annotation { "Feature Type Name" : "Feature", "Feature Type Description" : "" }
export const myFeature = defineFeature(function(context is Context, id is Id, definition is map)
    precondition{}
    {
        {
            var Q0;
            Q0=qCreatedBy(makeId("Top.planeOp"),FACE);
            var sketch = newSketch(context, id + "F0", { "sketchPlane" : qUnion([Q0])});
            skLineSegment(sketch, "E0.bottom", {"start": v(0, 0) * mm, "end": v(66.68, 0) * mm});
            skLineSegment(sketch, "E0.top", {"start": v(0, -53.98) * mm, "end": v(66.68, -53.98) * mm});
            skLineSegment(sketch, "E0.left", {"start": v(0, 0) * mm, "end": v(0, -53.98) * mm});
            skLineSegment(sketch, "E0.right", {"start": v(66.68, 0) * mm, "end": v(66.68, -53.97) * mm});
            skLineSegment(sketch, "E1.bottom", {"start": v(-2.38, -7.94) * mm, "end": v(5.56, -7.94) * mm});
            skLineSegment(sketch, "E1.top", {"start": v(-2.38, -15.08) * mm, "end": v(5.56, -15.08) * mm});
            skLineSegment(sketch, "E1.left", {"start": v(-2.38, -7.94) * mm, "end": v(-2.38, -15.08) * mm});
            skLineSegment(sketch, "E1.right", {"start": v(5.56, -7.94) * mm, "end": v(5.56, -15.08) * mm});
            skLineSegment(sketch, "E2", {"start": v(66.68, -12.7) * mm, "end": v(70.64, -16.67) * mm});
            skLineSegment(sketch, "E3", {"start": v(70.64, -16.67) * mm, "end": v(70.64, -48.42) * mm});
            skLineSegment(sketch, "E4", {"start": v(70.64, -48.42) * mm, "end": v(66.68, -52.39) * mm});
            skCircle(sketch, "E5", {"center": v(68.26, -19.05) * mm, "radius": 1.98 * mm});
            skLineSegment(sketch, "E6", {"start": v(66.68, -12.7) * mm, "end": v(68.26, -12.7) * mm, "construction": true});
            skLineSegment(sketch, "E7", {"start": v(68.26, -12.7) * mm, "end": v(68.26, -19.05) * mm, "construction": true});
            skLineSegment(sketch, "E8", {"start": v(70.64, -32.54) * mm, "end": v(66.68, -32.54) * mm});
            skCircle(sketch, "E9.MirrorC", {"center": v(68.26, -46.04) * mm, "radius": 1.98 * mm});
            skCircle(sketch, "E10", {"center": v(15.88, -2.38) * mm, "radius": 1.98 * mm});
            skLineSegment(sketch, "E11", {"start": v(0, -26.99) * mm, "end": v(15.88, -26.99) * mm, "construction": true});
            skCircle(sketch, "E12.MirrorC", {"center": v(15.88, -51.6) * mm, "radius": 1.98 * mm});
            skSolve(sketch);
        }
        {
            var Q0;
            {var subQ9=sQuery(id+"F0.wireOp",EDGE,"E0.bottom");Q0=makeQuery(id+"F0.imprint","IMPRINT",FACE,{"disambiguationData":[TD([[makeQuery(id+"F0.imprint","IMPRINT",EDGE,{"derivedFrom":subQ9}),-1.0]])]});}
            var Q1;
            {var subQ5=sQuery(id+"F0.wireOp",EDGE,"E2");Q1=makeQuery(id+"F0.imprint","IMPRINT",FACE,{"disambiguationData":[TD([[makeQuery(id+"F0.imprint","IMPRINT",EDGE,{"derivedFrom":subQ5}),-1.0]])]});}
            var Q2;
            {var subQ0=sQuery(id+"F0.wireOp",EDGE,"E4");Q2=makeQuery(id+"F0.imprint","IMPRINT",FACE,{"disambiguationData":[TD([[makeQuery(id+"F0.imprint","IMPRINT",EDGE,{"derivedFrom":subQ0}),-1.0]])]});}
            extrude(context, id + "F1", {"entities" : qUnion([Q0, Q1, Q2]), "depth" : 1.59 * mm});
        }
        {
            var Q0;
            {var subQ5=sQuery(id+"F0.wireOp",EDGE,"E1.right");Q0=makeQuery(id+"F0.imprint","IMPRINT",FACE,{"disambiguationData":[TD([[makeQuery(id+"F0.imprint","IMPRINT",EDGE,{"derivedFrom":subQ5}),-1.0]])]});}
            var Q1;
            {var subQ5=sQuery(id+"F0.wireOp",EDGE,"E1.left");Q1=makeQuery(id+"F0.imprint","IMPRINT",FACE,{"disambiguationData":[TD([[makeQuery(id+"F0.imprint","IMPRINT",EDGE,{"derivedFrom":subQ5}),1.0]])]});}
            extrude(context, id + "F2", {"entities" : qUnion([Q0, Q1]), "operationType" : NewBodyOperationType.ADD, "depth" : 5.16 * mm});
        }
        {
            var Q0;
            Q0=makeQuery(id+"F1.opExtrude","CAP_FACE",FACE,{"disambiguationData":[OSD([sQuery(id+"F0.wireOp",EDGE,"E0.bottom"),sQuery(id+"F0.wireOp",EDGE,"E0.top"),sQuery(id+"F0.wireOp",EDGE,"E0.left"),sQuery(id+"F0.wireOp",EDGE,"E0.right"),sQuery(id+"F0.wireOp",EDGE,"E1.bottom"),sQuery(id+"F0.wireOp",EDGE,"E1.top"),sQuery(id+"F0.wireOp",EDGE,"E1.right"),sQuery(id+"F0.wireOp",EDGE,"E2"),sQuery(id+"F0.wireOp",EDGE,"E3"),sQuery(id+"F0.wireOp",EDGE,"E4"),sQuery(id+"F0.wireOp",EDGE,"E5"),sQuery(id+"F0.wireOp",EDGE,"E9.MirrorC"),sQuery(id+"F0.wireOp",EDGE,"E10"),sQuery(id+"F0.wireOp",EDGE,"E12.MirrorC")])],"isStart":false});
            var sketch = newSketch(context, id + "F3", { "sketchPlane" : qUnion([Q0])});
            skLineSegment(sketch, "E13.bottom", {"start": v(31.75, -50) * mm, "end": v(46.83, -50) * mm});
            skLineSegment(sketch, "E13.top", {"start": v(31.75, -52.39) * mm, "end": v(46.83, -52.39) * mm});
            skLineSegment(sketch, "E13.left", {"start": v(31.75, -50) * mm, "end": v(31.75, -52.39) * mm});
            skLineSegment(sketch, "E13.right", {"start": v(46.83, -50) * mm, "end": v(46.83, -52.39) * mm});
            skLineSegment(sketch, "E14", {"start": v(48.02, -48.64) * mm, "end": v(48.02, -53.98) * mm, "construction": true});
            skLineSegment(sketch, "E15.MirrorCS", {"start": v(64.3, -50) * mm, "end": v(49.21, -50) * mm});
            skLineSegment(sketch, "E16.MirrorCS", {"start": v(49.21, -50) * mm, "end": v(49.21, -52.39) * mm});
            skLineSegment(sketch, "E17.MirrorCS", {"start": v(64.3, -52.39) * mm, "end": v(49.21, -52.39) * mm});
            skLineSegment(sketch, "E18.MirrorCS", {"start": v(64.3, -50) * mm, "end": v(64.3, -52.39) * mm});
            skLineSegment(sketch, "E19.bottom", {"start": v(32.35, -50.4) * mm, "end": v(33.93, -50.4) * mm});
            skLineSegment(sketch, "E19.top", {"start": v(32.35, -52) * mm, "end": v(33.93, -52) * mm});
            skLineSegment(sketch, "E19.left", {"start": v(32.35, -50.4) * mm, "end": v(32.35, -52) * mm});
            skLineSegment(sketch, "E19.right", {"start": v(33.93, -50.4) * mm, "end": v(33.93, -52) * mm});
            skLineSegment(sketch, "E20.bottom", {"start": v(34.77, -50.4) * mm, "end": v(36.36, -50.4) * mm});
            skLineSegment(sketch, "E20.top", {"start": v(34.77, -52) * mm, "end": v(36.36, -52) * mm});
            skLineSegment(sketch, "E20.left", {"start": v(34.77, -50.4) * mm, "end": v(34.77, -52) * mm});
            skLineSegment(sketch, "E20.right", {"start": v(36.36, -50.4) * mm, "end": v(36.36, -52) * mm});
            skLineSegment(sketch, "E21", {"start": v(36.8, -50) * mm, "end": v(36.8, -52.39) * mm, "construction": true});
            skLineSegment(sketch, "E22.MirrorCS", {"start": v(38.8, -50.4) * mm, "end": v(37.22, -50.4) * mm});
            skLineSegment(sketch, "E23.MirrorCS", {"start": v(37.22, -50.4) * mm, "end": v(37.22, -52) * mm});
            skLineSegment(sketch, "E24.MirrorCS", {"start": v(38.8, -52) * mm, "end": v(37.22, -52) * mm});
            skLineSegment(sketch, "E25.MirrorCS", {"start": v(38.8, -50.4) * mm, "end": v(38.8, -52) * mm});
            skLineSegment(sketch, "E26.MirrorCS", {"start": v(39.65, -50.4) * mm, "end": v(39.65, -52) * mm});
            skLineSegment(sketch, "E27.MirrorCS", {"start": v(41.24, -50.4) * mm, "end": v(39.65, -50.4) * mm});
            skLineSegment(sketch, "E28.MirrorCS", {"start": v(41.24, -50.4) * mm, "end": v(41.24, -52) * mm});
            skLineSegment(sketch, "E29.MirrorCS", {"start": v(41.24, -52) * mm, "end": v(39.65, -52) * mm});
            skLineSegment(sketch, "E30", {"start": v(41.67, -50) * mm, "end": v(41.67, -52.39) * mm, "construction": true});
            skLineSegment(sketch, "E31.MirrorCS", {"start": v(42.1, -50.4) * mm, "end": v(43.69, -50.4) * mm});
            skLineSegment(sketch, "E32.MirrorCS", {"start": v(42.1, -50.4) * mm, "end": v(42.1, -52) * mm});
            skLineSegment(sketch, "E33.MirrorCS", {"start": v(42.1, -52) * mm, "end": v(43.69, -52) * mm});
            skLineSegment(sketch, "E34.MirrorCS", {"start": v(43.69, -50.4) * mm, "end": v(43.69, -52) * mm});
            skLineSegment(sketch, "E35.MirrorCS", {"start": v(44.52, -50.4) * mm, "end": v(44.52, -52) * mm});
            skLineSegment(sketch, "E36.MirrorCS", {"start": v(44.52, -50.4) * mm, "end": v(46.11, -50.4) * mm});
            skLineSegment(sketch, "E37.MirrorCS", {"start": v(46.11, -50.4) * mm, "end": v(46.11, -52) * mm});
            skLineSegment(sketch, "E38.MirrorCS", {"start": v(44.52, -52) * mm, "end": v(46.11, -52) * mm});
            skLineSegment(sketch, "E39.MirrorCS", {"start": v(49.93, -50.4) * mm, "end": v(49.93, -52) * mm});
            skLineSegment(sketch, "E40.MirrorCS", {"start": v(51.52, -50.4) * mm, "end": v(49.93, -50.4) * mm});
            skLineSegment(sketch, "E41.MirrorCS", {"start": v(51.52, -50.4) * mm, "end": v(51.52, -52) * mm});
            skLineSegment(sketch, "E42.MirrorCS", {"start": v(51.52, -52) * mm, "end": v(49.93, -52) * mm});
            skLineSegment(sketch, "E43.MirrorCS", {"start": v(52.36, -50.4) * mm, "end": v(52.36, -52) * mm});
            skLineSegment(sketch, "E44.MirrorCS", {"start": v(53.94, -50.4) * mm, "end": v(52.36, -50.4) * mm});
            skLineSegment(sketch, "E45.MirrorCS", {"start": v(53.94, -50.4) * mm, "end": v(53.94, -52) * mm});
            skLineSegment(sketch, "E46.MirrorCS", {"start": v(53.94, -52) * mm, "end": v(52.36, -52) * mm});
            skLineSegment(sketch, "E47.MirrorCS", {"start": v(54.8, -50.4) * mm, "end": v(56.4, -50.4) * mm});
            skLineSegment(sketch, "E48.MirrorCS", {"start": v(54.8, -50.4) * mm, "end": v(54.8, -52) * mm});
            skLineSegment(sketch, "E49.MirrorCS", {"start": v(54.8, -52) * mm, "end": v(56.4, -52) * mm});
            skLineSegment(sketch, "E50.MirrorCS", {"start": v(56.4, -50.4) * mm, "end": v(56.4, -52) * mm});
            skLineSegment(sketch, "E51.MirrorCS", {"start": v(57.23, -50.4) * mm, "end": v(57.23, -52) * mm});
            skLineSegment(sketch, "E52.MirrorCS", {"start": v(57.23, -50.4) * mm, "end": v(58.82, -50.4) * mm});
            skLineSegment(sketch, "E53.MirrorCS", {"start": v(58.82, -50.4) * mm, "end": v(58.82, -52) * mm});
            skLineSegment(sketch, "E54.MirrorCS", {"start": v(57.23, -52) * mm, "end": v(58.82, -52) * mm});
            skLineSegment(sketch, "E55.MirrorCS", {"start": v(59.69, -50.4) * mm, "end": v(59.69, -52) * mm});
            skLineSegment(sketch, "E56.MirrorCS", {"start": v(61.27, -50.4) * mm, "end": v(59.69, -50.4) * mm});
            skLineSegment(sketch, "E57.MirrorCS", {"start": v(61.27, -50.4) * mm, "end": v(61.27, -52) * mm});
            skLineSegment(sketch, "E58.MirrorCS", {"start": v(61.27, -52) * mm, "end": v(59.69, -52) * mm});
            skLineSegment(sketch, "E59.MirrorCS", {"start": v(62.11, -50.4) * mm, "end": v(62.11, -52) * mm});
            skLineSegment(sketch, "E60.MirrorCS", {"start": v(63.7, -50.4) * mm, "end": v(62.11, -50.4) * mm});
            skLineSegment(sketch, "E61.MirrorCS", {"start": v(63.7, -50.4) * mm, "end": v(63.7, -52) * mm});
            skLineSegment(sketch, "E62.MirrorCS", {"start": v(63.7, -52) * mm, "end": v(62.11, -52) * mm});
            skSolve(sketch);
        }
        {
            var Q0;
            Q0=makeQuery(id+"F3.imprint","IMPRINT",FACE,{"disambiguationData":[TD([[makeQuery(id+"F3.imprint","IMPRINT",EDGE,{"derivedFrom":sQuery(id+"F3.wireOp",EDGE,"E13.bottom")}),-1.0]])]});
            var Q1;
            Q1=makeQuery(id+"F3.imprint","IMPRINT",FACE,{"disambiguationData":[TD([[makeQuery(id+"F3.imprint","IMPRINT",EDGE,{"derivedFrom":sQuery(id+"F3.wireOp",EDGE,"E15.MirrorCS")}),1.0]])]});
            extrude(context, id + "F4", {"entities" : qUnion([Q0, Q1]), "operationType" : NewBodyOperationType.ADD, "depth" : 7.94 * mm});
        }
        {
            var Q0;
            {var subQ0=sQuery(id+"F0.wireOp",EDGE,"E1.right");var subQ1=sQuery(id+"F0.wireOp",EDGE,"E0.left");var subQ2=sQuery(id+"F0.wireOp",EDGE,"E0.bottom");var subQ3=sQuery(id+"F0.wireOp",EDGE,"E1.bottom");var subQ4=sQuery(id+"F0.wireOp",EDGE,"E1.top");var subQ5=sQuery(id+"F0.wireOp",EDGE,"E12.MirrorC");var subQ6=sQuery(id+"F0.wireOp",EDGE,"E10");var subQ7=sQuery(id+"F0.wireOp",EDGE,"E9.MirrorC");var subQ8=sQuery(id+"F0.wireOp",EDGE,"E0.top");var subQ9=sQuery(id+"F0.wireOp",EDGE,"E3");var subQ10=sQuery(id+"F0.wireOp",EDGE,"E0.right");var subQ11=sQuery(id+"F0.wireOp",EDGE,"E2");var subQ12=sQuery(id+"F0.wireOp",EDGE,"E4");var subQ13=sQuery(id+"F0.wireOp",EDGE,"E5");Q0=makeQuery(id+"F4.boolean.opBoolean","SPLIT",FACE,{"disambiguationData":[TD([makeQuery(id+"F1.opExtrude","SWEPT_FACE",FACE,{"disambiguationData":[OSD([subQ2])]})])],"derivedFrom":makeQuery(id+"F1.opExtrude","CAP_FACE",FACE,{"disambiguationData":[OSD([subQ2,subQ8,subQ1,subQ10,subQ3,subQ4,subQ0,subQ11,subQ9,subQ12,subQ13,subQ7,subQ6,subQ5])],"isStart":false})});}
            var sketch = newSketch(context, id + "F5", { "sketchPlane" : qUnion([Q0])});
            skLineSegment(sketch, "E63.bottom", {"start": v(30.96, -34.13) * mm, "end": v(65.88, -34.13) * mm});
            skLineSegment(sketch, "E63.top", {"start": v(30.96, -42.86) * mm, "end": v(65.88, -42.86) * mm});
            skLineSegment(sketch, "E63.left", {"start": v(30.96, -34.13) * mm, "end": v(30.96, -42.86) * mm});
            skLineSegment(sketch, "E63.right", {"start": v(65.88, -34.13) * mm, "end": v(65.88, -42.86) * mm});
            skSolve(sketch);
        }
        {
            var Q0;
            Q0=makeQuery(id+"F5.imprint","IMPRINT",FACE,{"disambiguationData":[TD([[makeQuery(id+"F5.imprint","IMPRINT",EDGE,{"derivedFrom":sQuery(id+"F5.wireOp",EDGE,"E63.bottom")}),-1.0]])]});
            extrude(context, id + "F6", {"entities" : qUnion([Q0]), "operationType" : NewBodyOperationType.ADD, "depth" : 7.14 * mm});
        }
        {
            var Q0;
            {var subQ0=sQuery(id+"F0.wireOp",EDGE,"E1.right");var subQ1=sQuery(id+"F0.wireOp",EDGE,"E0.left");var subQ2=sQuery(id+"F0.wireOp",EDGE,"E0.bottom");var subQ3=sQuery(id+"F0.wireOp",EDGE,"E1.bottom");var subQ4=sQuery(id+"F0.wireOp",EDGE,"E1.top");var subQ5=sQuery(id+"F0.wireOp",EDGE,"E12.MirrorC");var subQ6=sQuery(id+"F0.wireOp",EDGE,"E10");var subQ7=sQuery(id+"F0.wireOp",EDGE,"E9.MirrorC");var subQ8=sQuery(id+"F0.wireOp",EDGE,"E0.top");var subQ9=sQuery(id+"F0.wireOp",EDGE,"E3");var subQ10=sQuery(id+"F0.wireOp",EDGE,"E0.right");var subQ11=sQuery(id+"F0.wireOp",EDGE,"E2");var subQ12=sQuery(id+"F0.wireOp",EDGE,"E4");var subQ13=sQuery(id+"F0.wireOp",EDGE,"E5");Q0=makeQuery(id+"F4.boolean.opBoolean","SPLIT",FACE,{"disambiguationData":[TD([makeQuery(id+"F1.opExtrude","SWEPT_FACE",FACE,{"disambiguationData":[OSD([subQ2])]})])],"derivedFrom":makeQuery(id+"F1.opExtrude","CAP_FACE",FACE,{"disambiguationData":[OSD([subQ2,subQ8,subQ1,subQ10,subQ3,subQ4,subQ0,subQ11,subQ9,subQ12,subQ13,subQ7,subQ6,subQ5])],"isStart":false})});}
            var sketch = newSketch(context, id + "F7", { "sketchPlane" : qUnion([Q0])});
            skLineSegment(sketch, "E64.bottom", {"start": v(53.98, -25.4) * mm, "end": v(59.53, -25.4) * mm});
            skLineSegment(sketch, "E64.top", {"start": v(53.98, -30.96) * mm, "end": v(59.53, -30.96) * mm});
            skLineSegment(sketch, "E64.left", {"start": v(53.98, -25.4) * mm, "end": v(53.98, -30.96) * mm});
            skLineSegment(sketch, "E64.right", {"start": v(59.53, -25.4) * mm, "end": v(59.53, -30.96) * mm});
            skSolve(sketch);
        }
        {
            var Q0;
            Q0=makeQuery(id+"F7.imprint","IMPRINT",FACE,{"disambiguationData":[TD([[makeQuery(id+"F7.imprint","IMPRINT",EDGE,{"derivedFrom":sQuery(id+"F7.wireOp",EDGE,"E64.bottom")}),-1.0]])]});
            extrude(context, id + "F8", {"entities" : qUnion([Q0]), "operationType" : NewBodyOperationType.ADD, "depth" : 2 / 406.4 * mm});
        }
        {
            var Q0;
            Q0=makeQuery(id+"F8.opExtrude","CAP_FACE",FACE,{"disambiguationData":[OSD([sQuery(id+"F7.wireOp",EDGE,"E64.bottom"),sQuery(id+"F7.wireOp",EDGE,"E64.top"),sQuery(id+"F7.wireOp",EDGE,"E64.left"),sQuery(id+"F7.wireOp",EDGE,"E64.right")])],"isStart":false});
            var sketch = newSketch(context, id + "F9", { "sketchPlane" : qUnion([Q0])});
            skCircle(sketch, "E65", {"center": v(56.75, -28.18) * mm, "radius": 1.98 * mm});
            skPoint(sketch, "E65.centerSnap0", {"position": v(59.53, -28.18) * mm});
            skPoint(sketch, "E65.centerSnap1", {"position": v(56.75, -25.4) * mm});
            skCircle(sketch, "E66", {"center": v(54.68, -26.1) * mm, "radius": 0.38 * mm});
            skCircle(sketch, "E67.1.0.0", {"center": v(58.8, -26.1) * mm, "radius": 0.38 * mm});
            skLineSegment(sketch, "E67.direction1", {"start": v(54.68, -26.1) * mm, "end": v(58.8, -26.1) * mm, "construction": true});
            skCircle(sketch, "E68.1.0.0", {"center": v(58.77, -30.28) * mm, "radius": 0.38 * mm});
            skLineSegment(sketch, "E68.direction1", {"start": v(58.8, -26.1) * mm, "end": v(58.77, -30.28) * mm, "construction": true});
            skCircle(sketch, "E69.1.0.0", {"center": v(54.73, -30.25) * mm, "radius": 0.38 * mm});
            skLineSegment(sketch, "E69.direction1", {"start": v(54.68, -26.1) * mm, "end": v(54.73, -30.25) * mm, "construction": true});
            skSolve(sketch);
        }
        {
            var Q0;
            Q0=makeQuery(id+"F9.imprint","IMPRINT",FACE,{"disambiguationData":[TD([[makeQuery(id+"F9.imprint","IMPRINT",EDGE,{"derivedFrom":sQuery(id+"F9.wireOp",EDGE,"E65")}),1.0]])]});
            extrude(context, id + "F10", {"entities" : qUnion([Q0]), "operationType" : NewBodyOperationType.ADD, "depth" : 0.8 * mm});
        }
        {
            var Q0;
            Q0=makeQuery(id+"F9.imprint","IMPRINT",FACE,{"disambiguationData":[TD([[makeQuery(id+"F9.imprint","IMPRINT",EDGE,{"derivedFrom":sQuery(id+"F9.wireOp",EDGE,"E66")}),1.0]])]});
            var Q1;
            Q1=makeQuery(id+"F9.imprint","IMPRINT",FACE,{"disambiguationData":[TD([[makeQuery(id+"F9.imprint","IMPRINT",EDGE,{"derivedFrom":sQuery(id+"F9.wireOp",EDGE,"E67.1.0.0")}),1.0]])]});
            var Q2;
            Q2=makeQuery(id+"F9.imprint","IMPRINT",FACE,{"disambiguationData":[TD([[makeQuery(id+"F9.imprint","IMPRINT",EDGE,{"derivedFrom":sQuery(id+"F9.wireOp",EDGE,"E68.1.0.0")}),1.0]])]});
            var Q3;
            Q3=makeQuery(id+"F9.imprint","IMPRINT",FACE,{"disambiguationData":[TD([[makeQuery(id+"F9.imprint","IMPRINT",EDGE,{"derivedFrom":sQuery(id+"F9.wireOp",EDGE,"E69.1.0.0")}),1.0]])]});
            extrude(context, id + "F11", {"entities" : qUnion([Q0, Q1, Q2, Q3]), "operationType" : NewBodyOperationType.ADD, "depth" : 0.2 * mm});
        }
        {
            var Q0;
            {var subQ0=sQuery(id+"F0.wireOp",EDGE,"E1.right");var subQ1=sQuery(id+"F0.wireOp",EDGE,"E0.left");var subQ2=sQuery(id+"F0.wireOp",EDGE,"E0.bottom");var subQ3=sQuery(id+"F0.wireOp",EDGE,"E1.bottom");var subQ4=sQuery(id+"F0.wireOp",EDGE,"E1.top");var subQ5=sQuery(id+"F0.wireOp",EDGE,"E12.MirrorC");var subQ6=sQuery(id+"F0.wireOp",EDGE,"E10");var subQ7=sQuery(id+"F0.wireOp",EDGE,"E9.MirrorC");var subQ8=sQuery(id+"F0.wireOp",EDGE,"E0.top");var subQ9=sQuery(id+"F0.wireOp",EDGE,"E3");var subQ10=sQuery(id+"F0.wireOp",EDGE,"E0.right");var subQ11=sQuery(id+"F0.wireOp",EDGE,"E2");var subQ12=sQuery(id+"F0.wireOp",EDGE,"E4");var subQ13=sQuery(id+"F0.wireOp",EDGE,"E5");Q0=makeQuery(id+"F4.boolean.opBoolean","SPLIT",FACE,{"disambiguationData":[TD([makeQuery(id+"F1.opExtrude","SWEPT_FACE",FACE,{"disambiguationData":[OSD([subQ2])]})])],"derivedFrom":makeQuery(id+"F1.opExtrude","CAP_FACE",FACE,{"disambiguationData":[OSD([subQ2,subQ8,subQ1,subQ10,subQ3,subQ4,subQ0,subQ11,subQ9,subQ12,subQ13,subQ7,subQ6,subQ5])],"isStart":false})});}
            var sketch = newSketch(context, id + "F12", { "sketchPlane" : qUnion([Q0])});
            skLineSegment(sketch, "E70.bottom", {"start": v(22.23, -1.6) * mm, "end": v(42.86, -1.6) * mm});
            skLineSegment(sketch, "E70.top", {"start": v(22.23, -3.99) * mm, "end": v(42.86, -3.99) * mm});
            skLineSegment(sketch, "E70.left", {"start": v(22.23, -1.6) * mm, "end": v(22.23, -3.99) * mm});
            skLineSegment(sketch, "E70.right", {"start": v(42.86, -1.6) * mm, "end": v(42.86, -3.99) * mm});
            skLineSegment(sketch, "E71.bottom", {"start": v(22.8, -2) * mm, "end": v(24.4, -2) * mm});
            skLineSegment(sketch, "E71.top", {"start": v(22.8, -3.6) * mm, "end": v(24.4, -3.6) * mm});
            skLineSegment(sketch, "E71.left", {"start": v(22.8, -2) * mm, "end": v(22.8, -3.6) * mm});
            skLineSegment(sketch, "E71.right", {"start": v(24.4, -2) * mm, "end": v(24.4, -3.6) * mm});
            skLineSegment(sketch, "E72", {"start": v(24.9, -1.6) * mm, "end": v(24.9, -3.99) * mm, "construction": true});
            skLineSegment(sketch, "E73.MirrorCS", {"start": v(25.37, -2) * mm, "end": v(25.37, -3.6) * mm});
            skLineSegment(sketch, "E74.MirrorCS", {"start": v(26.97, -2) * mm, "end": v(25.37, -2) * mm});
            skLineSegment(sketch, "E75.MirrorCS", {"start": v(26.97, -2) * mm, "end": v(26.97, -3.6) * mm});
            skLineSegment(sketch, "E76.MirrorCS", {"start": v(26.97, -3.6) * mm, "end": v(25.37, -3.6) * mm});
            skLineSegment(sketch, "E77", {"start": v(27.46, -1.6) * mm, "end": v(27.46, -3.99) * mm, "construction": true});
            skLineSegment(sketch, "E78.MirrorCS", {"start": v(27.94, -2) * mm, "end": v(27.94, -3.6) * mm});
            skLineSegment(sketch, "E79.MirrorCS", {"start": v(27.94, -2) * mm, "end": v(29.54, -2) * mm});
            skLineSegment(sketch, "E80.MirrorCS", {"start": v(29.54, -2) * mm, "end": v(29.54, -3.6) * mm});
            skLineSegment(sketch, "E81.MirrorCS", {"start": v(27.94, -3.6) * mm, "end": v(29.54, -3.6) * mm});
            skLineSegment(sketch, "E82.MirrorCS", {"start": v(30.5, -2) * mm, "end": v(30.5, -3.6) * mm});
            skLineSegment(sketch, "E83.MirrorCS", {"start": v(32.1, -2) * mm, "end": v(30.5, -2) * mm});
            skLineSegment(sketch, "E84.MirrorCS", {"start": v(32.1, -2) * mm, "end": v(32.1, -3.6) * mm});
            skLineSegment(sketch, "E85.MirrorCS", {"start": v(32.1, -3.6) * mm, "end": v(30.5, -3.6) * mm});
            skLineSegment(sketch, "E86", {"start": v(32.59, -1.6) * mm, "end": v(32.59, -3.99) * mm, "construction": true});
            skLineSegment(sketch, "E87.MirrorCS", {"start": v(33.07, -2) * mm, "end": v(33.07, -3.6) * mm});
            skLineSegment(sketch, "E88.MirrorCS", {"start": v(33.07, -2) * mm, "end": v(34.67, -2) * mm});
            skLineSegment(sketch, "E89.MirrorCS", {"start": v(34.67, -2) * mm, "end": v(34.67, -3.6) * mm});
            skLineSegment(sketch, "E90.MirrorCS", {"start": v(33.07, -3.6) * mm, "end": v(34.67, -3.6) * mm});
            skLineSegment(sketch, "E91.MirrorCS", {"start": v(35.64, -2) * mm, "end": v(35.64, -3.6) * mm});
            skLineSegment(sketch, "E92.MirrorCS", {"start": v(37.24, -2) * mm, "end": v(35.64, -2) * mm});
            skLineSegment(sketch, "E93.MirrorCS", {"start": v(37.24, -2) * mm, "end": v(37.24, -3.6) * mm});
            skLineSegment(sketch, "E94.MirrorCS", {"start": v(37.24, -3.6) * mm, "end": v(35.64, -3.6) * mm});
            skLineSegment(sketch, "E95.MirrorCS", {"start": v(38.2, -2) * mm, "end": v(38.2, -3.6) * mm});
            skLineSegment(sketch, "E96.MirrorCS", {"start": v(38.2, -2) * mm, "end": v(39.8, -2) * mm});
            skLineSegment(sketch, "E97.MirrorCS", {"start": v(39.8, -2) * mm, "end": v(39.8, -3.6) * mm});
            skLineSegment(sketch, "E98.MirrorCS", {"start": v(38.2, -3.6) * mm, "end": v(39.8, -3.6) * mm});
            skLineSegment(sketch, "E99.MirrorCS", {"start": v(40.77, -2) * mm, "end": v(40.77, -3.6) * mm});
            skLineSegment(sketch, "E100.MirrorCS", {"start": v(42.37, -2) * mm, "end": v(40.77, -2) * mm});
            skLineSegment(sketch, "E101.MirrorCS", {"start": v(42.37, -2) * mm, "end": v(42.37, -3.6) * mm});
            skLineSegment(sketch, "E102.MirrorCS", {"start": v(42.37, -3.6) * mm, "end": v(40.77, -3.6) * mm});
            skLineSegment(sketch, "E103", {"start": v(43.66, 0) * mm, "end": v(43.66, -3.99) * mm, "construction": true});
            skLineSegment(sketch, "E104.MirrorCS", {"start": v(44.45, -1.6) * mm, "end": v(44.45, -3.99) * mm});
            skLineSegment(sketch, "E105.MirrorCS", {"start": v(65.09, -1.6) * mm, "end": v(65.09, -3.99) * mm});
            skLineSegment(sketch, "E106.MirrorCS", {"start": v(65.09, -1.6) * mm, "end": v(44.45, -1.6) * mm});
            skLineSegment(sketch, "E107.MirrorCS", {"start": v(65.09, -3.99) * mm, "end": v(44.45, -3.99) * mm});
            skLineSegment(sketch, "E108.MirrorCS", {"start": v(44.95, -3.6) * mm, "end": v(46.55, -3.6) * mm});
            skLineSegment(sketch, "E109.MirrorCS", {"start": v(44.95, -2) * mm, "end": v(44.95, -3.6) * mm});
            skLineSegment(sketch, "E110.MirrorCS", {"start": v(44.95, -2) * mm, "end": v(46.55, -2) * mm});
            skLineSegment(sketch, "E111.MirrorCS", {"start": v(46.55, -2) * mm, "end": v(46.55, -3.6) * mm});
            skLineSegment(sketch, "E112.MirrorCS", {"start": v(47.51, -2) * mm, "end": v(47.51, -3.6) * mm});
            skLineSegment(sketch, "E113.MirrorCS", {"start": v(49.11, -2) * mm, "end": v(47.51, -2) * mm});
            skLineSegment(sketch, "E114.MirrorCS", {"start": v(49.11, -2) * mm, "end": v(49.11, -3.6) * mm});
            skLineSegment(sketch, "E115.MirrorCS", {"start": v(49.11, -3.6) * mm, "end": v(47.51, -3.6) * mm});
            skLineSegment(sketch, "E116.MirrorCS", {"start": v(50.08, -2) * mm, "end": v(50.08, -3.6) * mm});
            skLineSegment(sketch, "E117.MirrorCS", {"start": v(50.08, -2) * mm, "end": v(51.68, -2) * mm});
            skLineSegment(sketch, "E118.MirrorCS", {"start": v(51.68, -2) * mm, "end": v(51.68, -3.6) * mm});
            skLineSegment(sketch, "E119.MirrorCS", {"start": v(50.08, -3.6) * mm, "end": v(51.68, -3.6) * mm});
            skLineSegment(sketch, "E120.MirrorCS", {"start": v(52.64, -2) * mm, "end": v(52.64, -3.6) * mm});
            skLineSegment(sketch, "E121.MirrorCS", {"start": v(54.24, -2) * mm, "end": v(52.64, -2) * mm});
            skLineSegment(sketch, "E122.MirrorCS", {"start": v(54.24, -2) * mm, "end": v(54.24, -3.6) * mm});
            skLineSegment(sketch, "E123.MirrorCS", {"start": v(54.24, -3.6) * mm, "end": v(52.64, -3.6) * mm});
            skLineSegment(sketch, "E124.MirrorCS", {"start": v(55.2, -2) * mm, "end": v(55.2, -3.6) * mm});
            skLineSegment(sketch, "E125.MirrorCS", {"start": v(55.2, -2) * mm, "end": v(56.8, -2) * mm});
            skLineSegment(sketch, "E126.MirrorCS", {"start": v(56.8, -2) * mm, "end": v(56.8, -3.6) * mm});
            skLineSegment(sketch, "E127.MirrorCS", {"start": v(55.2, -3.6) * mm, "end": v(56.8, -3.6) * mm});
            skLineSegment(sketch, "E128.MirrorCS", {"start": v(57.77, -2) * mm, "end": v(57.77, -3.6) * mm});
            skLineSegment(sketch, "E129.MirrorCS", {"start": v(59.37, -2) * mm, "end": v(57.77, -2) * mm});
            skLineSegment(sketch, "E130.MirrorCS", {"start": v(59.37, -2) * mm, "end": v(59.37, -3.6) * mm});
            skLineSegment(sketch, "E131.MirrorCS", {"start": v(59.37, -3.6) * mm, "end": v(57.77, -3.6) * mm});
            skLineSegment(sketch, "E132.MirrorCS", {"start": v(60.34, -2) * mm, "end": v(60.34, -3.6) * mm});
            skLineSegment(sketch, "E133.MirrorCS", {"start": v(60.34, -2) * mm, "end": v(61.94, -2) * mm});
            skLineSegment(sketch, "E134.MirrorCS", {"start": v(61.94, -2) * mm, "end": v(61.94, -3.6) * mm});
            skLineSegment(sketch, "E135.MirrorCS", {"start": v(60.34, -3.6) * mm, "end": v(61.94, -3.6) * mm});
            skLineSegment(sketch, "E136.MirrorCS", {"start": v(62.9, -2) * mm, "end": v(62.9, -3.6) * mm});
            skLineSegment(sketch, "E137.MirrorCS", {"start": v(64.5, -2) * mm, "end": v(62.9, -2) * mm});
            skLineSegment(sketch, "E138.MirrorCS", {"start": v(64.5, -2) * mm, "end": v(64.5, -3.6) * mm});
            skLineSegment(sketch, "E139.MirrorCS", {"start": v(64.5, -3.6) * mm, "end": v(62.9, -3.6) * mm});
            skSolve(sketch);
        }
        {
            var Q0;
            Q0=makeQuery(id+"F12.imprint","IMPRINT",FACE,{"disambiguationData":[TD([[makeQuery(id+"F12.imprint","IMPRINT",EDGE,{"derivedFrom":sQuery(id+"F12.wireOp",EDGE,"E70.bottom")}),-1.0]])]});
            var Q1;
            Q1=makeQuery(id+"F12.imprint","IMPRINT",FACE,{"disambiguationData":[TD([[makeQuery(id+"F12.imprint","IMPRINT",EDGE,{"derivedFrom":sQuery(id+"F12.wireOp",EDGE,"E104.MirrorCS")}),1.0]])]});
            extrude(context, id + "F13", {"entities" : qUnion([Q0, Q1]), "operationType" : NewBodyOperationType.ADD, "depth" : 7.95 * mm});
        }
        {
            var Q0;
            {var subQ2=sQuery(id+"F0.wireOp",EDGE,"E1.right");var subQ4=sQuery(id+"F0.wireOp",EDGE,"E0.left");var subQ5=sQuery(id+"F0.wireOp",EDGE,"E0.bottom");var subQ6=sQuery(id+"F0.wireOp",EDGE,"E1.bottom");var subQ8=sQuery(id+"F0.wireOp",EDGE,"E1.top");var subQ10=sQuery(id+"F0.wireOp",EDGE,"E12.MirrorC");var subQ12=sQuery(id+"F0.wireOp",EDGE,"E10");var subQ14=sQuery(id+"F0.wireOp",EDGE,"E9.MirrorC");var subQ16=sQuery(id+"F0.wireOp",EDGE,"E0.top");var subQ18=sQuery(id+"F0.wireOp",EDGE,"E3");var subQ23=makeQuery(id+"F1.opExtrude","SWEPT_FACE",FACE,{"disambiguationData":[OSD([subQ5])]});var subQ24=sQuery(id+"F0.wireOp",EDGE,"E0.right");var subQ25=sQuery(id+"F0.wireOp",EDGE,"E2");var subQ28=sQuery(id+"F0.wireOp",EDGE,"E4");var subQ32=sQuery(id+"F0.wireOp",EDGE,"E5");Q0=makeQuery(id+"F13.boolean.opBoolean","SPLIT",FACE,{"disambiguationData":[TD([subQ23])],"derivedFrom":makeQuery(id+"F4.boolean.opBoolean","SPLIT",FACE,{"disambiguationData":[TD([subQ23])],"derivedFrom":makeQuery(id+"F1.opExtrude","CAP_FACE",FACE,{"disambiguationData":[OSD([subQ5,subQ16,subQ4,subQ24,subQ6,subQ8,subQ2,subQ25,subQ18,subQ28,subQ32,subQ14,subQ12,subQ10])],"isStart":false})})});}
            var sketch = newSketch(context, id + "F14", { "sketchPlane" : qUnion([Q0])});
            skCircle(sketch, "E140", {"center": v(21.43, -49.21) * mm, "radius": 2.78 * mm});
            skCircle(sketch, "E141", {"center": v(27.78, -49.21) * mm, "radius": 2.78 * mm});
            skLineSegment(sketch, "E142", {"start": v(24.87, -53.98) * mm, "end": v(32.2, -53.98) * mm, "construction": true});
            skSolve(sketch);
        }
        {
            var Q0;
            Q0=makeQuery(id+"F14.imprint","IMPRINT",FACE,{"disambiguationData":[TD([[makeQuery(id+"F14.imprint","IMPRINT",EDGE,{"derivedFrom":sQuery(id+"F14.wireOp",EDGE,"E140")}),1.0]])]});
            var Q1;
            Q1=makeQuery(id+"F14.imprint","IMPRINT",FACE,{"disambiguationData":[TD([[makeQuery(id+"F14.imprint","IMPRINT",EDGE,{"derivedFrom":sQuery(id+"F14.wireOp",EDGE,"E141")}),1.0]])]});
            extrude(context, id + "F15", {"entities" : qUnion([Q0, Q1]), "operationType" : NewBodyOperationType.ADD, "depth" : 4.5 / 406.4 * mm});
        }
        {
            var Q0;
            {var subQ2=sQuery(id+"F0.wireOp",EDGE,"E1.right");var subQ4=sQuery(id+"F0.wireOp",EDGE,"E0.left");var subQ5=sQuery(id+"F0.wireOp",EDGE,"E0.bottom");var subQ6=sQuery(id+"F0.wireOp",EDGE,"E1.bottom");var subQ8=sQuery(id+"F0.wireOp",EDGE,"E1.top");var subQ10=sQuery(id+"F0.wireOp",EDGE,"E12.MirrorC");var subQ12=sQuery(id+"F0.wireOp",EDGE,"E10");var subQ14=sQuery(id+"F0.wireOp",EDGE,"E9.MirrorC");var subQ16=sQuery(id+"F0.wireOp",EDGE,"E0.top");var subQ18=sQuery(id+"F0.wireOp",EDGE,"E3");var subQ23=makeQuery(id+"F1.opExtrude","SWEPT_FACE",FACE,{"disambiguationData":[OSD([subQ5])]});var subQ24=sQuery(id+"F0.wireOp",EDGE,"E0.right");var subQ25=sQuery(id+"F0.wireOp",EDGE,"E2");var subQ28=sQuery(id+"F0.wireOp",EDGE,"E4");var subQ32=sQuery(id+"F0.wireOp",EDGE,"E5");Q0=makeQuery(id+"F13.boolean.opBoolean","SPLIT",FACE,{"disambiguationData":[TD([subQ23])],"derivedFrom":makeQuery(id+"F4.boolean.opBoolean","SPLIT",FACE,{"disambiguationData":[TD([subQ23])],"derivedFrom":makeQuery(id+"F1.opExtrude","CAP_FACE",FACE,{"disambiguationData":[OSD([subQ5,subQ16,subQ4,subQ24,subQ6,subQ8,subQ2,subQ25,subQ18,subQ28,subQ32,subQ14,subQ12,subQ10])],"isStart":false})})});}
            var sketch = newSketch(context, id + "F16", { "sketchPlane" : qUnion([Q0])});
            skLineSegment(sketch, "E143.bottom", {"start": v(0, -19.84) * mm, "end": v(3.97, -19.84) * mm});
            skLineSegment(sketch, "E143.top", {"start": v(0, -31.75) * mm, "end": v(3.97, -31.75) * mm});
            skLineSegment(sketch, "E143.left", {"start": v(0, -19.84) * mm, "end": v(0, -31.75) * mm});
            skLineSegment(sketch, "E143.right", {"start": v(3.97, -19.84) * mm, "end": v(3.97, -31.75) * mm});
            skSolve(sketch);
        }
        {
            var Q0;
            Q0=makeQuery(id+"F16.imprint","IMPRINT",FACE,{"disambiguationData":[TD([[makeQuery(id+"F16.imprint","IMPRINT",EDGE,{"derivedFrom":sQuery(id+"F16.wireOp",EDGE,"E143.bottom")}),-1.0]])]});
            extrude(context, id + "F17", {"entities" : qUnion([Q0]), "operationType" : NewBodyOperationType.ADD, "depth" : 5.16 * mm});
        }
        {
            var Q0;
            Q0=makeQuery(id+"F17.opExtrude","CAP_FACE",FACE,{"disambiguationData":[OSD([sQuery(id+"F16.wireOp",EDGE,"E143.bottom"),sQuery(id+"F16.wireOp",EDGE,"E143.top"),sQuery(id+"F16.wireOp",EDGE,"E143.left"),sQuery(id+"F16.wireOp",EDGE,"E143.right")])],"isStart":false});
            var sketch = newSketch(context, id + "F18", { "sketchPlane" : qUnion([Q0])});
            skLineSegment(sketch, "E144.bottom", {"start": v(0.8, -23.42) * mm, "end": v(3.18, -23.42) * mm});
            skLineSegment(sketch, "E144.top", {"start": v(0.8, -28.18) * mm, "end": v(3.18, -28.18) * mm});
            skLineSegment(sketch, "E144.left", {"start": v(0.8, -23.42) * mm, "end": v(0.8, -28.18) * mm});
            skLineSegment(sketch, "E144.right", {"start": v(3.18, -23.42) * mm, "end": v(3.18, -28.18) * mm});
            skSolve(sketch);
        }
        {
            var Q0;
            Q0=makeQuery(id+"F18.imprint","IMPRINT",FACE,{"disambiguationData":[TD([[makeQuery(id+"F18.imprint","IMPRINT",EDGE,{"derivedFrom":sQuery(id+"F18.wireOp",EDGE,"E144.bottom")}),-1.0]])]});
            extrude(context, id + "F19", {"entities" : qUnion([Q0]), "operationType" : NewBodyOperationType.REMOVE, "oppositeDirection" : true, "depth" : 1.2 * mm});
        }
        {
            var Q0;
            Q0=makeQuery(id+"F19.boolean.opBoolean","COPY",FACE,{"derivedFrom":makeQuery(id+"F19.opExtrude","CAP_FACE",FACE,{"disambiguationData":[OSD([sQuery(id+"F18.wireOp",EDGE,"E144.bottom"),sQuery(id+"F18.wireOp",EDGE,"E144.top"),sQuery(id+"F18.wireOp",EDGE,"E144.left"),sQuery(id+"F18.wireOp",EDGE,"E144.right")])],"isStart":false})});
            var sketch = newSketch(context, id + "F20", { "sketchPlane" : qUnion([Q0])});
            skLineSegment(sketch, "E145.bottom", {"start": v(0.8, -26.27) * mm, "end": v(3.17, -26.27) * mm});
            skLineSegment(sketch, "E145.top", {"start": v(0.8, -28.18) * mm, "end": v(3.17, -28.18) * mm});
            skLineSegment(sketch, "E145.left", {"start": v(0.8, -26.27) * mm, "end": v(0.8, -28.18) * mm});
            skLineSegment(sketch, "E145.right", {"start": v(3.17, -26.27) * mm, "end": v(3.17, -28.18) * mm});
            skSolve(sketch);
        }
        {
            var Q0;
            Q0=makeQuery(id+"F20.imprint","IMPRINT",FACE,{"disambiguationData":[TD([[makeQuery(id+"F20.imprint","IMPRINT",EDGE,{"derivedFrom":sQuery(id+"F20.wireOp",EDGE,"E145.bottom")}),-1.0]])]});
            extrude(context, id + "F21", {"entities" : qUnion([Q0]), "operationType" : NewBodyOperationType.ADD, "depth" : 3.17 * mm});
        }
        {
            var Q0;
            {var subQ0=sQuery(id+"F0.wireOp",EDGE,"E1.right");var subQ1=sQuery(id+"F0.wireOp",EDGE,"E1.top");var subQ2=sQuery(id+"F0.wireOp",EDGE,"E1.bottom");Q0=makeQuery(id+"F2.boolean.opBoolean","MERGE",FACE,{"derivedFrom":[makeQuery(id+"F1.opExtrude","CAP_FACE",FACE,{"disambiguationData":[OSD([sQuery(id+"F0.wireOp",EDGE,"E0.bottom"),sQuery(id+"F0.wireOp",EDGE,"E0.top"),sQuery(id+"F0.wireOp",EDGE,"E0.left"),sQuery(id+"F0.wireOp",EDGE,"E0.right"),subQ2,subQ1,subQ0,sQuery(id+"F0.wireOp",EDGE,"E2"),sQuery(id+"F0.wireOp",EDGE,"E3"),sQuery(id+"F0.wireOp",EDGE,"E4"),sQuery(id+"F0.wireOp",EDGE,"E5"),sQuery(id+"F0.wireOp",EDGE,"E9.MirrorC"),sQuery(id+"F0.wireOp",EDGE,"E10"),sQuery(id+"F0.wireOp",EDGE,"E12.MirrorC")])],"isStart":true}),makeQuery(id+"F2.opExtrude","CAP_FACE",FACE,{"disambiguationData":[OSD([subQ2,subQ1,sQuery(id+"F0.wireOp",EDGE,"E1.left"),subQ0])],"isStart":true})]});}
            var sketch = newSketch(context, id + "F22", { "sketchPlane" : qUnion([Q0])});
            skText(sketch, "E146", { "text": "Grace Qi\nSuresh Patil\n6P", "fontName": "OpenSans-Regular.ttf"});
            const initialGuessF22  = {"E146": [0.01217, 0.03678, 1, 0, 0.00543]};
            skSetInitialGuess(sketch, initialGuessF22);
            skSolve(sketch);
        }
        {
            var Q0;
            Q0 = qSketchRegion(id + "F22", true);
            extrude(context, id + "F23", {"entities" : qUnion([Q0]), "operationType" : NewBodyOperationType.REMOVE, "oppositeDirection" : true, "depth" : 0.2 * mm});
        }
        {
            var Q0;
            Q0=makeQuery(id+"F2.opExtrude","SWEPT_FACE",FACE,{"disambiguationData":[OSD([sQuery(id+"F0.wireOp",EDGE,"E1.left")])]});
            var sketch = newSketch(context, id + "F24", { "sketchPlane" : qUnion([Q0])});
            skLineSegment(sketch, "E147.bottom", {"start": v(8.45, 4.65) * mm, "end": v(14.57, 4.65) * mm});
            skLineSegment(sketch, "E147.top", {"start": v(8.45, 2.1) * mm, "end": v(14.57, 2.1) * mm});
            skLineSegment(sketch, "E147.left", {"start": v(8.45, 4.65) * mm, "end": v(8.45, 2.1) * mm});
            skLineSegment(sketch, "E147.right", {"start": v(14.57, 4.65) * mm, "end": v(14.57, 2.1) * mm});
            skLineSegment(sketch, "E148.bottom", {"start": v(9.46, 3.64) * mm, "end": v(13.56, 3.64) * mm});
            skLineSegment(sketch, "E148.top", {"start": v(9.46, 2.73) * mm, "end": v(13.56, 2.73) * mm});
            skLineSegment(sketch, "E148.left", {"start": v(9.46, 3.64) * mm, "end": v(9.46, 2.73) * mm});
            skLineSegment(sketch, "E148.right", {"start": v(13.56, 3.64) * mm, "end": v(13.56, 2.73) * mm});
            skLineSegment(sketch, "E149.bottom", {"start": v(7.94, 1.58) * mm, "end": v(15.08, 1.58) * mm});
            skLineSegment(sketch, "E149.top", {"start": v(7.94, 0) * mm, "end": v(15.08, 0) * mm});
            skLineSegment(sketch, "E149.left", {"start": v(7.94, 1.58) * mm, "end": v(7.94, 0) * mm});
            skLineSegment(sketch, "E149.right", {"start": v(15.08, 1.58) * mm, "end": v(15.08, 0) * mm});
            skSolve(sketch);
        }
        {
            var Q0;
            Q0=makeQuery(id+"F24.imprint","IMPRINT",FACE,{"disambiguationData":[TD([[makeQuery(id+"F24.imprint","IMPRINT",EDGE,{"derivedFrom":sQuery(id+"F24.wireOp",EDGE,"E147.bottom")}),-1.0]])]});
            extrude(context, id + "F25", {"entities" : qUnion([Q0]), "operationType" : NewBodyOperationType.REMOVE, "oppositeDirection" : true, "depth" : 7.14 * mm});
        }
        {
            var Q0;
            Q0=makeQuery(id+"F25.boolean.opBoolean","SPLIT",FACE,{"disambiguationData":[TD([makeQuery(id+"F25.opExtrude","SWEPT_FACE",FACE,{"disambiguationData":[OSD([sQuery(id+"F24.wireOp",EDGE,"E148.bottom")])]})])],"derivedFrom":makeQuery(id+"F2.opExtrude","SWEPT_FACE",FACE,{"disambiguationData":[OSD([sQuery(id+"F0.wireOp",EDGE,"E1.left")])]})});
            extrude(context, id + "F26", {"entities" : qUnion([Q0]), "operationType" : NewBodyOperationType.REMOVE, "oppositeDirection" : true, "depth" : 0.76 * mm});
        }
        {
            var Q0;
            Q0=makeQuery(id+"F26.boolean.opBoolean","COPY",FACE,{"derivedFrom":makeQuery(id+"F26.opExtrude","CAP_FACE",FACE,{"disambiguationData":[OSD([sQuery(id+"F0.wireOp",EDGE,"E1.left")])],"isStart":false})});
            var sketch = newSketch(context, id + "F27", { "sketchPlane" : qUnion([Q0])});
            skCircle(sketch, "E150", {"center": v(10.21, 3.2) * mm, "radius": 0.2 * mm});
            skCircle(sketch, "E151", {"center": v(10.88, 3.2) * mm, "radius": 0.2 * mm});
            skCircle(sketch, "E152", {"center": v(11.5, 3.2) * mm, "radius": 0.2 * mm});
            skCircle(sketch, "E153", {"center": v(12.12, 3.2) * mm, "radius": 0.2 * mm});
            skCircle(sketch, "E154", {"center": v(12.8, 3.2) * mm, "radius": 0.2 * mm});
            skSolve(sketch);
        }
        {
            var Q0;
            Q0=makeQuery(id+"F27.imprint","IMPRINT",FACE,{"disambiguationData":[TD([[makeQuery(id+"F27.imprint","IMPRINT",EDGE,{"derivedFrom":sQuery(id+"F27.wireOp",EDGE,"E150")}),1.0]])]});
            var Q1;
            Q1=makeQuery(id+"F27.imprint","IMPRINT",FACE,{"disambiguationData":[TD([[makeQuery(id+"F27.imprint","IMPRINT",EDGE,{"derivedFrom":sQuery(id+"F27.wireOp",EDGE,"E151")}),1.0]])]});
            var Q2;
            Q2=makeQuery(id+"F27.imprint","IMPRINT",FACE,{"disambiguationData":[TD([[makeQuery(id+"F27.imprint","IMPRINT",EDGE,{"derivedFrom":sQuery(id+"F27.wireOp",EDGE,"E152")}),1.0]])]});
            var Q3;
            Q3=makeQuery(id+"F27.imprint","IMPRINT",FACE,{"disambiguationData":[TD([[makeQuery(id+"F27.imprint","IMPRINT",EDGE,{"derivedFrom":sQuery(id+"F27.wireOp",EDGE,"E153")}),1.0]])]});
            var Q4;
            Q4=makeQuery(id+"F27.imprint","IMPRINT",FACE,{"disambiguationData":[TD([[makeQuery(id+"F27.imprint","IMPRINT",EDGE,{"derivedFrom":sQuery(id+"F27.wireOp",EDGE,"E154")}),1.0]])]});
            extrude(context, id + "F28", {"entities" : qUnion([Q0, Q1, Q2, Q3, Q4]), "operationType" : NewBodyOperationType.REMOVE, "oppositeDirection" : true, "depth" : 5.56 * mm});
        }
        {
            var Q0;
            Q0=makeQuery(id+"F24.imprint","IMPRINT",FACE,{"disambiguationData":[TD([[makeQuery(id+"F24.imprint","IMPRINT",EDGE,{"derivedFrom":sQuery(id+"F24.wireOp",EDGE,"E149.bottom")}),-1.0]])]});
            extrude(context, id + "F29", {"entities" : qUnion([Q0]), "operationType" : NewBodyOperationType.REMOVE, "oppositeDirection" : true, "depth" : 2.4 * mm});
        }
        {
            var Q0;
            {var subQ0=sQuery(id+"F0.wireOp",EDGE,"E0.left");Q0=makeQuery(id+"F17.boolean.opBoolean","MERGE",FACE,{"derivedFrom":[makeQuery(id+"F1.opExtrude","SWEPT_FACE",FACE,{"disambiguationData":[OSD([subQ0]),TDD([makeQuery(id+"F0.imprint","IMPRINT",EDGE,{"disambiguationData":[TD([[makeQuery(id+"F0.imprint","INTERSECT",VERTEX,{"derivedFrom":[sQuery(id+"F0.wireOp",EDGE,"E0.top"),subQ0]}),1.0]])],"derivedFrom":subQ0})])]}),makeQuery(id+"F17.opExtrude","SWEPT_FACE",FACE,{"disambiguationData":[OSD([sQuery(id+"F16.wireOp",EDGE,"E143.left")])]})]});}
            var sketch = newSketch(context, id + "F30", { "sketchPlane" : qUnion([Q0])});
            skLineSegment(sketch, "E155.bottom", {"start": v(50.8, 1.59) * mm, "end": v(42.07, 1.59) * mm});
            skLineSegment(sketch, "E155.top", {"start": v(50.8, 7.94) * mm, "end": v(42.07, 7.94) * mm});
            skLineSegment(sketch, "E155.left", {"start": v(50.8, 1.59) * mm, "end": v(50.8, 7.94) * mm});
            skLineSegment(sketch, "E155.right", {"start": v(42.07, 1.59) * mm, "end": v(42.07, 7.94) * mm});
            skCircle(sketch, "E156", {"center": v(46.43, 7.94) * mm, "radius": 4.39 * mm});
            skSolve(sketch);
        }
        {
            var Q0;
            {var subQ0=sQuery(id+"F30.wireOp",EDGE,"E155.top");Q0=makeQuery(id+"F30.imprint","IMPRINT",FACE,{"disambiguationData":[TD([[makeQuery(id+"F30.imprint","IMPRINT",EDGE,{"derivedFrom":subQ0}),-1.0]])]});}
            var Q1;
            {var subQ0=sQuery(id+"F30.wireOp",EDGE,"E155.top");Q1=makeQuery(id+"F30.imprint","IMPRINT",FACE,{"disambiguationData":[TD([[makeQuery(id+"F30.imprint","IMPRINT",EDGE,{"derivedFrom":subQ0}),1.0]])]});}
            var Q2;
            {var subQ0=sQuery(id+"F30.wireOp",EDGE,"E155.bottom");Q2=makeQuery(id+"F30.imprint","IMPRINT",FACE,{"disambiguationData":[TD([[makeQuery(id+"F30.imprint","IMPRINT",EDGE,{"derivedFrom":subQ0}),1.0]])]});}
            extrude(context, id + "F31", {"entities" : qUnion([Q0, Q1, Q2]), "operationType" : NewBodyOperationType.ADD, "oppositeDirection" : true, "depth" : 11.1 * mm});
        }
        {
            var Q0;
            {var subQ0=sQuery(id+"F0.wireOp",EDGE,"E0.left");Q0=makeQuery(id+"F31.boolean.opBoolean","MERGE",FACE,{"derivedFrom":[makeQuery(id+"F17.boolean.opBoolean","MERGE",FACE,{"derivedFrom":[makeQuery(id+"F1.opExtrude","SWEPT_FACE",FACE,{"disambiguationData":[OSD([subQ0]),TDD([makeQuery(id+"F0.imprint","IMPRINT",EDGE,{"disambiguationData":[TD([[makeQuery(id+"F0.imprint","INTERSECT",VERTEX,{"derivedFrom":[sQuery(id+"F0.wireOp",EDGE,"E0.top"),subQ0]}),1.0]])],"derivedFrom":subQ0})])]}),makeQuery(id+"F17.opExtrude","SWEPT_FACE",FACE,{"disambiguationData":[OSD([sQuery(id+"F16.wireOp",EDGE,"E143.left")])]})]}),makeQuery(id+"F31.opExtrude","CAP_FACE",FACE,{"disambiguationData":[OSD([sQuery(id+"F30.wireOp",EDGE,"E155.bottom"),sQuery(id+"F30.wireOp",EDGE,"E155.left"),sQuery(id+"F30.wireOp",EDGE,"E155.right"),sQuery(id+"F30.wireOp",EDGE,"E156")])],"isStart":true})]});}
            var sketch = newSketch(context, id + "F32", { "sketchPlane" : qUnion([Q0])});
            skLineSegment(sketch, "E157", {"start": v(42.07, 12.32) * mm, "end": v(50.8, 12.32) * mm, "construction": true});
            skPoint(sketch, "E157.startSnap0", {"position": v(46.43, 12.32) * mm});
            skPoint(sketch, "E157.endSnap0", {"position": v(46.43, 12.32) * mm});
            skLineSegment(sketch, "E158.bottom", {"start": v(42.07, 12.32) * mm, "end": v(50.8, 12.32) * mm});
            skLineSegment(sketch, "E158.top", {"start": v(42.07, 1.59) * mm, "end": v(50.8, 1.59) * mm});
            skLineSegment(sketch, "E158.left", {"start": v(42.07, 12.32) * mm, "end": v(42.07, 1.59) * mm});
            skLineSegment(sketch, "E158.right", {"start": v(50.8, 12.32) * mm, "end": v(50.8, 1.59) * mm});
            skSolve(sketch);
        }
        {
            var Q0;
            {var subQ0=sQuery(id+"F32.wireOp",EDGE,"E158.left");var subQ1=sQuery(id+"F32.wireOp",EDGE,"E158.bottom");var subQ2=makeQuery(id+"F32.imprint","INTERSECT",VERTEX,{"derivedFrom":[subQ1,subQ0]});Q0=makeQuery(id+"F32.imprint","IMPRINT",FACE,{"disambiguationData":[TD([[makeQuery(id+"F32.imprint","IMPRINT",EDGE,{"disambiguationData":[TD([[subQ2,-1.0]])],"derivedFrom":subQ1}),-1.0]])]});}
            var Q1;
            {var subQ5=sQuery(id+"F32.wireOp",EDGE,"E158.top");Q1=makeQuery(id+"F32.imprint","IMPRINT",FACE,{"disambiguationData":[TD([[makeQuery(id+"F32.imprint","IMPRINT",EDGE,{"derivedFrom":subQ5}),1.0]])]});}
            var Q2;
            {var subQ0=sQuery(id+"F32.wireOp",EDGE,"E158.right");var subQ1=sQuery(id+"F32.wireOp",EDGE,"E158.bottom");var subQ2=makeQuery(id+"F32.imprint","INTERSECT",VERTEX,{"derivedFrom":[subQ1,subQ0]});Q2=makeQuery(id+"F32.imprint","IMPRINT",FACE,{"disambiguationData":[TD([[makeQuery(id+"F32.imprint","IMPRINT",EDGE,{"disambiguationData":[TD([[subQ2,1.0]])],"derivedFrom":subQ1}),-1.0]])]});}
            extrude(context, id + "F33", {"entities" : qUnion([Q0, Q1, Q2]), "operationType" : NewBodyOperationType.ADD, "depth" : 3.17 * mm});
        }
        {
            var Q0;
            Q0=makeQuery(id+"F33.opExtrude","CAP_FACE",FACE,{"disambiguationData":[OSD([sQuery(id+"F32.wireOp",EDGE,"E158.bottom"),sQuery(id+"F32.wireOp",EDGE,"E158.top"),sQuery(id+"F32.wireOp",EDGE,"E158.left"),sQuery(id+"F32.wireOp",EDGE,"E158.right")])],"isStart":false});
            var sketch = newSketch(context, id + "F34", { "sketchPlane" : qUnion([Q0])});
            skCircle(sketch, "E159", {"center": v(46.43, 7.96) * mm, "radius": 2.78 * mm});
            skCircle(sketch, "E160", {"center": v(46.43, 7.96) * mm, "radius": 0.64 * mm});
            skSolve(sketch);
        }
        {
            var Q0;
            Q0=makeQuery(id+"F34.imprint","IMPRINT",FACE,{"disambiguationData":[TD([[makeQuery(id+"F34.imprint","IMPRINT",EDGE,{"derivedFrom":sQuery(id+"F34.wireOp",EDGE,"E159")}),1.0]])]});
            extrude(context, id + "F35", {"entities" : qUnion([Q0]), "operationType" : NewBodyOperationType.REMOVE, "oppositeDirection" : true, "depth" : 9.52 * mm});
        }
        {
            var Q0;
            Q0=makeQuery(id+"F35.boolean.opBoolean","SPLIT",FACE,{"disambiguationData":[TD([makeQuery(id+"F35.opExtrude","SWEPT_FACE",FACE,{"disambiguationData":[OSD([sQuery(id+"F34.wireOp",EDGE,"E160")])]})])],"derivedFrom":makeQuery(id+"F33.opExtrude","CAP_FACE",FACE,{"disambiguationData":[OSD([sQuery(id+"F32.wireOp",EDGE,"E158.bottom"),sQuery(id+"F32.wireOp",EDGE,"E158.top"),sQuery(id+"F32.wireOp",EDGE,"E158.left"),sQuery(id+"F32.wireOp",EDGE,"E158.right")])],"isStart":false})});
            extrude(context, id + "F36", {"entities" : qUnion([Q0]), "operationType" : NewBodyOperationType.REMOVE, "oppositeDirection" : true, "depth" : 1.59 * mm});
        }
        {
            var Q0;
            {var subQ3=sQuery(id+"F0.wireOp",EDGE,"E1.right");var subQ5=sQuery(id+"F0.wireOp",EDGE,"E0.left");var subQ6=sQuery(id+"F0.wireOp",EDGE,"E0.bottom");var subQ7=sQuery(id+"F0.wireOp",EDGE,"E1.bottom");var subQ9=sQuery(id+"F0.wireOp",EDGE,"E1.top");var subQ11=sQuery(id+"F0.wireOp",EDGE,"E12.MirrorC");var subQ13=sQuery(id+"F0.wireOp",EDGE,"E10");var subQ16=sQuery(id+"F0.wireOp",EDGE,"E9.MirrorC");var subQ18=sQuery(id+"F0.wireOp",EDGE,"E0.top");var subQ22=sQuery(id+"F0.wireOp",EDGE,"E3");var subQ25=makeQuery(id+"F1.opExtrude","SWEPT_FACE",FACE,{"disambiguationData":[OSD([subQ6])]});var subQ26=sQuery(id+"F0.wireOp",EDGE,"E0.right");var subQ27=sQuery(id+"F0.wireOp",EDGE,"E2");var subQ29=sQuery(id+"F0.wireOp",EDGE,"E4");var subQ32=sQuery(id+"F0.wireOp",EDGE,"E5");Q0=makeQuery(id+"F13.boolean.opBoolean","SPLIT",FACE,{"disambiguationData":[TD([subQ25])],"derivedFrom":makeQuery(id+"F4.boolean.opBoolean","SPLIT",FACE,{"disambiguationData":[TD([subQ25])],"derivedFrom":makeQuery(id+"F1.opExtrude","CAP_FACE",FACE,{"disambiguationData":[OSD([subQ6,subQ18,subQ5,subQ26,subQ7,subQ9,subQ3,subQ27,subQ22,subQ29,subQ32,subQ16,subQ13,subQ11])],"isStart":false})})});}
            var sketch = newSketch(context, id + "F37", { "sketchPlane" : qUnion([Q0])});
            skLineSegment(sketch, "E161.bottom", {"start": v(2.38, -34.13) * mm, "end": v(7.94, -34.13) * mm});
            skLineSegment(sketch, "E161.top", {"start": v(2.38, -39.69) * mm, "end": v(7.94, -39.69) * mm});
            skLineSegment(sketch, "E161.left", {"start": v(2.38, -34.13) * mm, "end": v(2.38, -39.69) * mm});
            skLineSegment(sketch, "E161.right", {"start": v(7.94, -34.13) * mm, "end": v(7.94, -39.69) * mm});
            skLineSegment(sketch, "E162.bottom", {"start": v(13.5, -9.13) * mm, "end": v(23.02, -9.13) * mm});
            skLineSegment(sketch, "E162.top", {"start": v(13.5, -13.9) * mm, "end": v(23.02, -13.9) * mm});
            skLineSegment(sketch, "E162.left", {"start": v(13.5, -9.13) * mm, "end": v(13.5, -13.9) * mm});
            skLineSegment(sketch, "E162.right", {"start": v(23.02, -9.13) * mm, "end": v(23.02, -13.9) * mm});
            skLineSegment(sketch, "E163.bottom", {"start": v(42.07, -23.37) * mm, "end": v(45.24, -23.37) * mm});
            skLineSegment(sketch, "E163.top", {"start": v(42.07, -29.72) * mm, "end": v(45.24, -29.72) * mm});
            skLineSegment(sketch, "E163.left", {"start": v(42.07, -23.37) * mm, "end": v(42.07, -29.72) * mm});
            skLineSegment(sketch, "E163.right", {"start": v(45.24, -23.37) * mm, "end": v(45.24, -29.72) * mm});
            skSolve(sketch);
        }
        {
            var Q0;
            Q0=makeQuery(id+"F37.imprint","IMPRINT",FACE,{"disambiguationData":[TD([[makeQuery(id+"F37.imprint","IMPRINT",EDGE,{"derivedFrom":sQuery(id+"F37.wireOp",EDGE,"E161.bottom")}),-1.0]])]});
            extrude(context, id + "F38", {"entities" : qUnion([Q0]), "operationType" : NewBodyOperationType.ADD, "depth" : 2.38 * mm});
        }
        {
            var Q0;
            Q0=makeQuery(id+"F37.imprint","IMPRINT",FACE,{"disambiguationData":[TD([[makeQuery(id+"F37.imprint","IMPRINT",EDGE,{"derivedFrom":sQuery(id+"F37.wireOp",EDGE,"E162.bottom")}),-1.0]])]});
            extrude(context, id + "F39", {"entities" : qUnion([Q0]), "operationType" : NewBodyOperationType.ADD, "depth" : 1.59 * mm});
        }
        {
            var Q0;
            Q0=makeQuery(id+"F37.imprint","IMPRINT",FACE,{"disambiguationData":[TD([[makeQuery(id+"F37.imprint","IMPRINT",EDGE,{"derivedFrom":sQuery(id+"F37.wireOp",EDGE,"E163.bottom")}),-1.0]])]});
            extrude(context, id + "F40", {"entities" : qUnion([Q0]), "operationType" : NewBodyOperationType.ADD, "depth" : 0.8 * mm});
        }
        {
            var Q0;
            {var subQ3=sQuery(id+"F0.wireOp",EDGE,"E1.right");var subQ5=sQuery(id+"F0.wireOp",EDGE,"E0.left");var subQ6=sQuery(id+"F0.wireOp",EDGE,"E0.bottom");var subQ7=sQuery(id+"F0.wireOp",EDGE,"E1.bottom");var subQ9=sQuery(id+"F0.wireOp",EDGE,"E1.top");var subQ11=sQuery(id+"F0.wireOp",EDGE,"E12.MirrorC");var subQ13=sQuery(id+"F0.wireOp",EDGE,"E10");var subQ16=sQuery(id+"F0.wireOp",EDGE,"E9.MirrorC");var subQ18=sQuery(id+"F0.wireOp",EDGE,"E0.top");var subQ22=sQuery(id+"F0.wireOp",EDGE,"E3");var subQ25=makeQuery(id+"F1.opExtrude","SWEPT_FACE",FACE,{"disambiguationData":[OSD([subQ6])]});var subQ26=sQuery(id+"F0.wireOp",EDGE,"E0.right");var subQ27=sQuery(id+"F0.wireOp",EDGE,"E2");var subQ29=sQuery(id+"F0.wireOp",EDGE,"E4");var subQ32=sQuery(id+"F0.wireOp",EDGE,"E5");Q0=makeQuery(id+"F13.boolean.opBoolean","SPLIT",FACE,{"disambiguationData":[TD([subQ25])],"derivedFrom":makeQuery(id+"F4.boolean.opBoolean","SPLIT",FACE,{"disambiguationData":[TD([subQ25])],"derivedFrom":makeQuery(id+"F1.opExtrude","CAP_FACE",FACE,{"disambiguationData":[OSD([subQ6,subQ18,subQ5,subQ26,subQ7,subQ9,subQ3,subQ27,subQ22,subQ29,subQ32,subQ16,subQ13,subQ11])],"isStart":false})})});}
            var sketch = newSketch(context, id + "F41", { "sketchPlane" : qUnion([Q0])});
            skLineSegment(sketch, "E164.bottom", {"start": v(4.76, -23.81) * mm, "end": v(6.75, -23.81) * mm});
            skLineSegment(sketch, "E164.top", {"start": v(4.76, -30.16) * mm, "end": v(6.75, -30.16) * mm});
            skLineSegment(sketch, "E164.left", {"start": v(4.76, -23.81) * mm, "end": v(4.76, -30.16) * mm});
            skLineSegment(sketch, "E164.right", {"start": v(6.75, -23.81) * mm, "end": v(6.75, -30.16) * mm});
            skLineSegment(sketch, "E165", {"start": v(6.48, -23.81) * mm, "end": v(6.75, -24.08) * mm});
            skLineSegment(sketch, "E166", {"start": v(6.75, -25.66) * mm, "end": v(6.48, -25.93) * mm});
            skLineSegment(sketch, "E167", {"start": v(6.48, -25.93) * mm, "end": v(6.75, -26.2) * mm});
            skLineSegment(sketch, "E168", {"start": v(6.75, -27.78) * mm, "end": v(6.48, -28.05) * mm});
            skLineSegment(sketch, "E169", {"start": v(6.48, -28.05) * mm, "end": v(6.75, -28.31) * mm});
            skLineSegment(sketch, "E170", {"start": v(6.75, -29.9) * mm, "end": v(6.48, -30.16) * mm});
            skLineSegment(sketch, "E171", {"start": v(5.75, -23.81) * mm, "end": v(5.75, -30.16) * mm, "construction": true});
            skLineSegment(sketch, "E172.MirrorCS", {"start": v(5.03, -23.81) * mm, "end": v(4.76, -24.08) * mm});
            skLineSegment(sketch, "E173.MirrorCS", {"start": v(4.76, -25.66) * mm, "end": v(5.03, -25.93) * mm});
            skLineSegment(sketch, "E174.MirrorCS", {"start": v(5.03, -25.93) * mm, "end": v(4.76, -26.2) * mm});
            skLineSegment(sketch, "E175.MirrorCS", {"start": v(4.76, -27.78) * mm, "end": v(5.03, -28.05) * mm});
            skLineSegment(sketch, "E176.MirrorCS", {"start": v(5.03, -28.05) * mm, "end": v(4.76, -28.31) * mm});
            skLineSegment(sketch, "E177.MirrorCS", {"start": v(4.76, -29.9) * mm, "end": v(5.03, -30.16) * mm});
            skSolve(sketch);
        }
        {
            var Q0;
            {var subQ0=sQuery(id+"F41.wireOp",EDGE,"E165");Q0=makeQuery(id+"F41.imprint","IMPRINT",FACE,{"disambiguationData":[TD([[makeQuery(id+"F41.imprint","IMPRINT",EDGE,{"derivedFrom":subQ0}),-1.0]])]});}
            extrude(context, id + "F42", {"entities" : qUnion([Q0]), "operationType" : NewBodyOperationType.ADD, "depth" : 2.38 * mm});
        }
        {
            var Q0;
            Q0=makeQuery(id+"F42.opExtrude","CAP_FACE",FACE,{"disambiguationData":[OSD([sQuery(id+"F41.wireOp",EDGE,"E164.bottom"),sQuery(id+"F41.wireOp",EDGE,"E164.top"),sQuery(id+"F41.wireOp",EDGE,"E164.left"),sQuery(id+"F41.wireOp",EDGE,"E164.right"),sQuery(id+"F41.wireOp",EDGE,"E165"),sQuery(id+"F41.wireOp",EDGE,"E166"),sQuery(id+"F41.wireOp",EDGE,"E167"),sQuery(id+"F41.wireOp",EDGE,"E168"),sQuery(id+"F41.wireOp",EDGE,"E169"),sQuery(id+"F41.wireOp",EDGE,"E170"),sQuery(id+"F41.wireOp",EDGE,"E172.MirrorCS"),sQuery(id+"F41.wireOp",EDGE,"E173.MirrorCS"),sQuery(id+"F41.wireOp",EDGE,"E174.MirrorCS"),sQuery(id+"F41.wireOp",EDGE,"E175.MirrorCS"),sQuery(id+"F41.wireOp",EDGE,"E176.MirrorCS"),sQuery(id+"F41.wireOp",EDGE,"E177.MirrorCS")])],"isStart":false});
            var sketch = newSketch(context, id + "F43", { "sketchPlane" : qUnion([Q0])});
            skLineSegment(sketch, "E178.bottom", {"start": v(4.76, -23.81) * mm, "end": v(6.75, -23.81) * mm});
            skLineSegment(sketch, "E178.top", {"start": v(4.76, -28.05) * mm, "end": v(6.75, -28.05) * mm});
            skLineSegment(sketch, "E178.left", {"start": v(4.76, -23.81) * mm, "end": v(4.76, -28.05) * mm});
            skLineSegment(sketch, "E178.right", {"start": v(6.75, -23.81) * mm, "end": v(6.75, -28.05) * mm});
            skSolve(sketch);
        }
        {
            var Q0;
            {var subQ1=makeQuery(id+"F42.opExtrude","CAP_EDGE",EDGE,{"disambiguationData":[OSD([sQuery(id+"F41.wireOp",EDGE,"E168")])],"isStart":false});Q0=makeQuery(id+"F43.imprint","IMPRINT",FACE,{"disambiguationData":[TD([[makeQuery(id+"F43.imprint","IMPRINT",EDGE,{"derivedFrom":subQ1}),1.0]])]});}
            var Q1;
            {var subQ1=makeQuery(id+"F42.opExtrude","CAP_EDGE",EDGE,{"disambiguationData":[OSD([sQuery(id+"F41.wireOp",EDGE,"E175.MirrorCS")])],"isStart":false});Q1=makeQuery(id+"F43.imprint","IMPRINT",FACE,{"disambiguationData":[TD([[makeQuery(id+"F43.imprint","IMPRINT",EDGE,{"derivedFrom":subQ1}),-1.0]])]});}
            var Q2;
            {var subQ1=makeQuery(id+"F42.opExtrude","CAP_EDGE",EDGE,{"disambiguationData":[OSD([sQuery(id+"F41.wireOp",EDGE,"E173.MirrorCS")])],"isStart":false});Q2=makeQuery(id+"F43.imprint","IMPRINT",FACE,{"disambiguationData":[TD([[makeQuery(id+"F43.imprint","IMPRINT",EDGE,{"derivedFrom":subQ1}),-1.0]])]});}
            var Q3;
            {var subQ1=makeQuery(id+"F42.opExtrude","CAP_EDGE",EDGE,{"disambiguationData":[OSD([sQuery(id+"F41.wireOp",EDGE,"E166")])],"isStart":false});Q3=makeQuery(id+"F43.imprint","IMPRINT",FACE,{"disambiguationData":[TD([[makeQuery(id+"F43.imprint","IMPRINT",EDGE,{"derivedFrom":subQ1}),1.0]])]});}
            var Q4;
            {var subQ2=makeQuery(id+"F42.opExtrude","CAP_EDGE",EDGE,{"disambiguationData":[OSD([sQuery(id+"F41.wireOp",EDGE,"E165")])],"isStart":false});Q4=makeQuery(id+"F43.imprint","IMPRINT",FACE,{"disambiguationData":[TD([[makeQuery(id+"F43.imprint","IMPRINT",EDGE,{"derivedFrom":subQ2}),-1.0]])]});}
            var Q5;
            {var subQ1=makeQuery(id+"F42.opExtrude","CAP_EDGE",EDGE,{"disambiguationData":[OSD([sQuery(id+"F41.wireOp",EDGE,"E165")])],"isStart":false});Q5=makeQuery(id+"F43.imprint","IMPRINT",FACE,{"disambiguationData":[TD([[makeQuery(id+"F43.imprint","IMPRINT",EDGE,{"derivedFrom":subQ1}),1.0]])]});}
            var Q6;
            {var subQ1=makeQuery(id+"F42.opExtrude","CAP_EDGE",EDGE,{"disambiguationData":[OSD([sQuery(id+"F41.wireOp",EDGE,"E172.MirrorCS")])],"isStart":false});Q6=makeQuery(id+"F43.imprint","IMPRINT",FACE,{"disambiguationData":[TD([[makeQuery(id+"F43.imprint","IMPRINT",EDGE,{"derivedFrom":subQ1}),-1.0]])]});}
            extrude(context, id + "F44", {"entities" : qUnion([Q0, Q1, Q2, Q3, Q4, Q5, Q6]), "operationType" : NewBodyOperationType.ADD, "depth" : 6.35 * mm});
        }
        {
            var Q0;
            Q0=makeQuery(id+"F42.opExtrude","CAP_FACE",FACE,{"disambiguationData":[OSD([sQuery(id+"F41.wireOp",EDGE,"E164.bottom"),sQuery(id+"F41.wireOp",EDGE,"E164.top"),sQuery(id+"F41.wireOp",EDGE,"E164.left"),sQuery(id+"F41.wireOp",EDGE,"E164.right"),sQuery(id+"F41.wireOp",EDGE,"E165"),sQuery(id+"F41.wireOp",EDGE,"E166"),sQuery(id+"F41.wireOp",EDGE,"E167"),sQuery(id+"F41.wireOp",EDGE,"E168"),sQuery(id+"F41.wireOp",EDGE,"E169"),sQuery(id+"F41.wireOp",EDGE,"E170"),sQuery(id+"F41.wireOp",EDGE,"E172.MirrorCS"),sQuery(id+"F41.wireOp",EDGE,"E173.MirrorCS"),sQuery(id+"F41.wireOp",EDGE,"E174.MirrorCS"),sQuery(id+"F41.wireOp",EDGE,"E175.MirrorCS"),sQuery(id+"F41.wireOp",EDGE,"E176.MirrorCS"),sQuery(id+"F41.wireOp",EDGE,"E177.MirrorCS")])],"isStart":false});
            var sketch = newSketch(context, id + "F45", { "sketchPlane" : qUnion([Q0])});
            skPoint(sketch, "E179", {"position": v(5.75, -29.1) * mm});
            skPoint(sketch, "E179.positionSnap0", {"position": v(4.76, -29.1) * mm});
            skPoint(sketch, "E179.positionSnap1", {"position": v(5.75, -28.05) * mm});
            skLineSegment(sketch, "E180.bottom", {"start": v(5.55, -28.92) * mm, "end": v(5.93, -28.92) * mm});
            skLineSegment(sketch, "E180.top", {"start": v(5.55, -29.3) * mm, "end": v(5.93, -29.3) * mm});
            skLineSegment(sketch, "E180.left", {"start": v(5.55, -28.92) * mm, "end": v(5.55, -29.3) * mm});
            skLineSegment(sketch, "E180.right", {"start": v(5.93, -28.92) * mm, "end": v(5.93, -29.3) * mm});
            skSolve(sketch);
        }
        {
            var Q0;
            Q0=makeQuery(id+"F45.imprint","IMPRINT",FACE,{"disambiguationData":[TD([[makeQuery(id+"F45.imprint","IMPRINT",EDGE,{"derivedFrom":sQuery(id+"F45.wireOp",EDGE,"E180.bottom")}),-1.0]])]});
            extrude(context, id + "F46", {"entities" : qUnion([Q0]), "operationType" : NewBodyOperationType.ADD, "depth" : 5.56 * mm});
        }
        {
            var Q0;
            {var subQ3=sQuery(id+"F0.wireOp",EDGE,"E1.right");var subQ5=sQuery(id+"F0.wireOp",EDGE,"E0.left");var subQ6=sQuery(id+"F0.wireOp",EDGE,"E0.bottom");var subQ7=sQuery(id+"F0.wireOp",EDGE,"E1.bottom");var subQ9=sQuery(id+"F0.wireOp",EDGE,"E1.top");var subQ11=sQuery(id+"F0.wireOp",EDGE,"E12.MirrorC");var subQ13=sQuery(id+"F0.wireOp",EDGE,"E10");var subQ16=sQuery(id+"F0.wireOp",EDGE,"E9.MirrorC");var subQ18=sQuery(id+"F0.wireOp",EDGE,"E0.top");var subQ22=sQuery(id+"F0.wireOp",EDGE,"E3");var subQ25=makeQuery(id+"F1.opExtrude","SWEPT_FACE",FACE,{"disambiguationData":[OSD([subQ6])]});var subQ26=sQuery(id+"F0.wireOp",EDGE,"E0.right");var subQ27=sQuery(id+"F0.wireOp",EDGE,"E2");var subQ29=sQuery(id+"F0.wireOp",EDGE,"E4");var subQ32=sQuery(id+"F0.wireOp",EDGE,"E5");Q0=makeQuery(id+"F13.boolean.opBoolean","SPLIT",FACE,{"disambiguationData":[TD([subQ25])],"derivedFrom":makeQuery(id+"F4.boolean.opBoolean","SPLIT",FACE,{"disambiguationData":[TD([subQ25])],"derivedFrom":makeQuery(id+"F1.opExtrude","CAP_FACE",FACE,{"disambiguationData":[OSD([subQ6,subQ18,subQ5,subQ26,subQ7,subQ9,subQ3,subQ27,subQ22,subQ29,subQ32,subQ16,subQ13,subQ11])],"isStart":false})})});}
            var sketch = newSketch(context, id + "F47", { "sketchPlane" : qUnion([Q0])});
            skCircle(sketch, "E181", {"center": v(5.56, -17.46) * mm, "radius": 1.2 * mm});
            skPoint(sketch, "E182.startSnap0", {"position": v(5.56, -11.5) * mm});
            skCircle(sketch, "E183.MirrorC", {"center": v(5.56, -5.56) * mm, "radius": 1.2 * mm});
            skCircle(sketch, "E184", {"center": v(7.54, -10.27) * mm, "radius": 0.6 * mm});
            skCircle(sketch, "E185", {"center": v(7.54, -12.65) * mm, "radius": 0.6 * mm});
            skLineSegment(sketch, "E186", {"start": v(8.73, -9.08) * mm, "end": v(8.73, -13.96) * mm, "construction": true});
            skCircle(sketch, "E187.MirrorC", {"center": v(9.92, -10.27) * mm, "radius": 0.6 * mm});
            skCircle(sketch, "E188.MirrorC", {"center": v(9.92, -12.65) * mm, "radius": 0.6 * mm});
            skPoint(sketch, "E189.endSnap0", {"position": v(7.94, -36.9) * mm});
            skCircle(sketch, "E190", {"center": v(13.9, -34.84) * mm, "radius": 0.6 * mm});
            skCircle(sketch, "E191", {"center": v(13.9, -37.22) * mm, "radius": 0.6 * mm});
            skLineSegment(sketch, "E192", {"start": v(7.94, -36.9) * mm, "end": v(14.76, -36.9) * mm, "construction": true});
            skCircle(sketch, "E193", {"center": v(13.9, -39.6) * mm, "radius": 0.6 * mm});
            skCircle(sketch, "E194", {"center": v(24.2, -10.32) * mm, "radius": 0.6 * mm});
            skCircle(sketch, "E195", {"center": v(24.2, -7.94) * mm, "radius": 0.6 * mm});
            skLineSegment(sketch, "E196", {"start": v(19.72, 0) * mm, "end": v(28.7, 0) * mm, "construction": true});
            skCircle(sketch, "E197", {"center": v(24.2, -12.7) * mm, "radius": 0.6 * mm});
            skCircle(sketch, "E198", {"center": v(24.2, -15.08) * mm, "radius": 0.6 * mm});
            skSolve(sketch);
        }
        {
            var Q0;
            Q0=makeQuery(id+"F47.imprint","IMPRINT",FACE,{"disambiguationData":[TD([[makeQuery(id+"F47.imprint","IMPRINT",EDGE,{"derivedFrom":sQuery(id+"F47.wireOp",EDGE,"E183.MirrorC")}),-1.0]])]});
            var Q1;
            Q1=makeQuery(id+"F47.imprint","IMPRINT",FACE,{"disambiguationData":[TD([[makeQuery(id+"F47.imprint","IMPRINT",EDGE,{"derivedFrom":sQuery(id+"F47.wireOp",EDGE,"E181")}),1.0]])]});
            var Q2;
            Q2=makeQuery(id+"F47.imprint","IMPRINT",FACE,{"disambiguationData":[TD([[makeQuery(id+"F47.imprint","IMPRINT",EDGE,{"derivedFrom":sQuery(id+"F47.wireOp",EDGE,"E185")}),1.0]])]});
            var Q3;
            Q3=makeQuery(id+"F47.imprint","IMPRINT",FACE,{"disambiguationData":[TD([[makeQuery(id+"F47.imprint","IMPRINT",EDGE,{"derivedFrom":sQuery(id+"F47.wireOp",EDGE,"E188.MirrorC")}),-1.0]])]});
            var Q4;
            Q4=makeQuery(id+"F47.imprint","IMPRINT",FACE,{"disambiguationData":[TD([[makeQuery(id+"F47.imprint","IMPRINT",EDGE,{"derivedFrom":sQuery(id+"F47.wireOp",EDGE,"E187.MirrorC")}),-1.0]])]});
            var Q5;
            Q5=makeQuery(id+"F47.imprint","IMPRINT",FACE,{"disambiguationData":[TD([[makeQuery(id+"F47.imprint","IMPRINT",EDGE,{"derivedFrom":sQuery(id+"F47.wireOp",EDGE,"E184")}),1.0]])]});
            var Q6;
            Q6=makeQuery(id+"F47.imprint","IMPRINT",FACE,{"disambiguationData":[TD([[makeQuery(id+"F47.imprint","IMPRINT",EDGE,{"derivedFrom":sQuery(id+"F47.wireOp",EDGE,"E191")}),1.0]])]});
            var Q7;
            Q7=makeQuery(id+"F47.imprint","IMPRINT",FACE,{"disambiguationData":[TD([[makeQuery(id+"F47.imprint","IMPRINT",EDGE,{"derivedFrom":sQuery(id+"F47.wireOp",EDGE,"E190")}),1.0]])]});
            var Q8;
            Q8=makeQuery(id+"F47.imprint","IMPRINT",FACE,{"disambiguationData":[TD([[makeQuery(id+"F47.imprint","IMPRINT",EDGE,{"derivedFrom":sQuery(id+"F47.wireOp",EDGE,"E193")}),1.0]])]});
            var Q9;
            Q9=makeQuery(id+"F47.imprint","IMPRINT",FACE,{"disambiguationData":[TD([[makeQuery(id+"F47.imprint","IMPRINT",EDGE,{"derivedFrom":sQuery(id+"F47.wireOp",EDGE,"E194")}),1.0]])]});
            var Q10;
            Q10=makeQuery(id+"F47.imprint","IMPRINT",FACE,{"disambiguationData":[TD([[makeQuery(id+"F47.imprint","IMPRINT",EDGE,{"derivedFrom":sQuery(id+"F47.wireOp",EDGE,"E195")}),1.0]])]});
            var Q11;
            Q11=makeQuery(id+"F47.imprint","IMPRINT",FACE,{"disambiguationData":[TD([[makeQuery(id+"F47.imprint","IMPRINT",EDGE,{"derivedFrom":sQuery(id+"F47.wireOp",EDGE,"E197")}),1.0]])]});
            var Q12;
            Q12=makeQuery(id+"F47.imprint","IMPRINT",FACE,{"disambiguationData":[TD([[makeQuery(id+"F47.imprint","IMPRINT",EDGE,{"derivedFrom":sQuery(id+"F47.wireOp",EDGE,"E198")}),1.0]])]});
            extrude(context, id + "F48", {"entities" : qUnion([Q0, Q1, Q2, Q3, Q4, Q5, Q6, Q7, Q8, Q9, Q10, Q11, Q12]), "operationType" : NewBodyOperationType.REMOVE, "oppositeDirection" : true, "depth" : 1.59 * mm});
        }
        {
            var Q0;
            Q0=makeQuery(id+"F6.opExtrude","SWEPT_FACE",FACE,{"disambiguationData":[OSD([sQuery(id+"F5.wireOp",EDGE,"E63.right")])]});
            var sketch = newSketch(context, id + "F49", { "sketchPlane" : qUnion([Q0])});
            skLineSegment(sketch, "E199.bottom", {"start": v(-42.86, 8.73) * mm, "end": v(-41.97, 8.73) * mm});
            skLineSegment(sketch, "E199.top", {"start": v(-42.86, 6.57) * mm, "end": v(-41.97, 6.57) * mm});
            skLineSegment(sketch, "E199.left", {"start": v(-42.86, 8.73) * mm, "end": v(-42.86, 6.57) * mm});
            skLineSegment(sketch, "E199.right", {"start": v(-41.97, 8.73) * mm, "end": v(-41.97, 6.57) * mm});
            skLineSegment(sketch, "E200", {"start": v(-38.5, 8.73) * mm, "end": v(-38.5, 5.45) * mm, "construction": true});
            skLineSegment(sketch, "E201.MirrorCS", {"start": v(-35.02, 8.73) * mm, "end": v(-35.02, 6.57) * mm});
            skLineSegment(sketch, "E202.MirrorCS", {"start": v(-34.13, 6.57) * mm, "end": v(-35.02, 6.57) * mm});
            skSolve(sketch);
        }
        {
            var Q0;
            Q0=makeQuery(id+"F49.imprint","IMPRINT",FACE,{"disambiguationData":[TD([[makeQuery(id+"F49.imprint","IMPRINT",EDGE,{"derivedFrom":sQuery(id+"F49.wireOp",EDGE,"E199.bottom")}),1.0]])]});
            var Q1;
            {var subQ0=sQuery(id+"F49.wireOp",EDGE,"E201.MirrorCS");Q1=makeQuery(id+"F49.imprint","IMPRINT",FACE,{"disambiguationData":[TD([[makeQuery(id+"F49.imprint","IMPRINT",EDGE,{"derivedFrom":subQ0}),1.0]])]});}
            extrude(context, id + "F50", {"entities" : qUnion([Q0, Q1]), "operationType" : NewBodyOperationType.REMOVE, "oppositeDirection" : true, "depth" : 34.92 * mm});
        }
    });